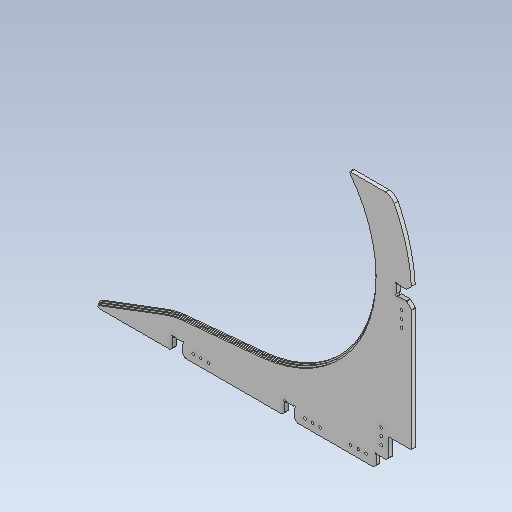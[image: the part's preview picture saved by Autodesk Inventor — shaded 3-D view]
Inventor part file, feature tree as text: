
AUTODESK INVENTOR PART (.ipt)
format: ipt  version: 2020 (Build 240168000, 168)  size: 361,472 bytes
history: native  units: in
note: dims shown in document units (in); Inventor stores cm internally (conversion verified against a paired STEP export)
features: extrude x4, sketch x4, fillet x2
ambient origin geometry x8: Origin, YZ Plane, XZ Plane, XY Plane, X Axis, Y Axis, Z Axis, Center Point
bodies: Solid1 (feature_tree)
feature tree (10):
  extrude  "Extrusion1"  Depth=1.0in
  fillet  "Fillet1"  Radius=11.0in
  extrude  "Extrusion2"  Depth=16.0in
  fillet  "Fillet2"  Radius=16.0in
  extrude  "Extrusion3"  Depth=7.25in
  extrude  "Extrusion4"  Depth=23.5in
  sketch  "Sketch1"  dims[d0=24.5in d1=1.0in d2=11.0in]
  sketch  "Sketch2"  dims[d3=9.0in d4=7.5in d5=16.0in]
  sketch  "Sketch3"  dims[d6=0.5in d7=7.25in]
  sketch  "Sketch4"  dims[d8=0.5in d9=23.5in d10=3.06in d11=24.0in d12=16.0in d13=1.0in d14=0.375in d15=0.0in d16=0.0in d17=2.0in d18=7.0in d19=1.0in d20=0.25in d21=0.0625in d22=0.2656in d23=1.0in d24=0.5in d25=1.0in d26=2.5in d27=1.1811in d29=0.75in d30=0.3937in d32=1.0in d34=1.0in d35=0.5in d36=0.5in d37=2.5in d38=1.1811in d40=0.75in d41=0.3937in d43=1.0in d45=0.175in d46=0.0in d47=0.0in d48=0.0625in d49=0.125in d50=0.25in d51=0.0in d52=0.125in d53=0.125in d54=0.0in]
